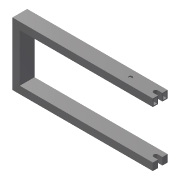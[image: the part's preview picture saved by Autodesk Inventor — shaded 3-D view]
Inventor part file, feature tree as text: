
AUTODESK INVENTOR PART (.ipt)
format: ipt  version: 2015 (Build 190159000, 159)  size: 154,624 bytes
history: native  units: mm
features: shell x2, sweep x1, extrude x1, hole x1, sketch x1
ambient origin geometry x8: Origin, YZ Plane, XZ Plane, XY Plane, X Axis, Y Axis, Z Axis, Center Point
bodies: Solid1 (feature_tree)
feature tree (6):
  sweep  "Sweep1"
  extrude  "Extrusion1"  Depth=20.0mm
  shell  "Shell1"  Thickness=0.0mm
  shell  "Shell2"  Thickness=12.0mm
  hole  "Hole1"  [1 undecoded]
  sketch  "Sketch1"  dims[d7=370.0mm d8=150.0mm d9=370.0mm d12=0.0mm d13=0.0mm d14=12.0mm d15=12.0mm d16=10.0mm d17=0.0mm d20=20.0mm d21=10.0mm d22=40.0mm d23=20.0mm d24=40.0mm d25=3.0mm d26=2.5mm d27=2.5mm d28=20.0mm d29=80.0mm d30=10.0mm d31=6.0mm d32=4.0mm d33=2.0mm d34=90.0deg d35=20.0mm d36=20.594885mm]
note: 1 required parameter value undecoded (feature->parameter linkage not recoverable at this tier; creation-order binding heuristic only, values carry confidence <= 0.55)
